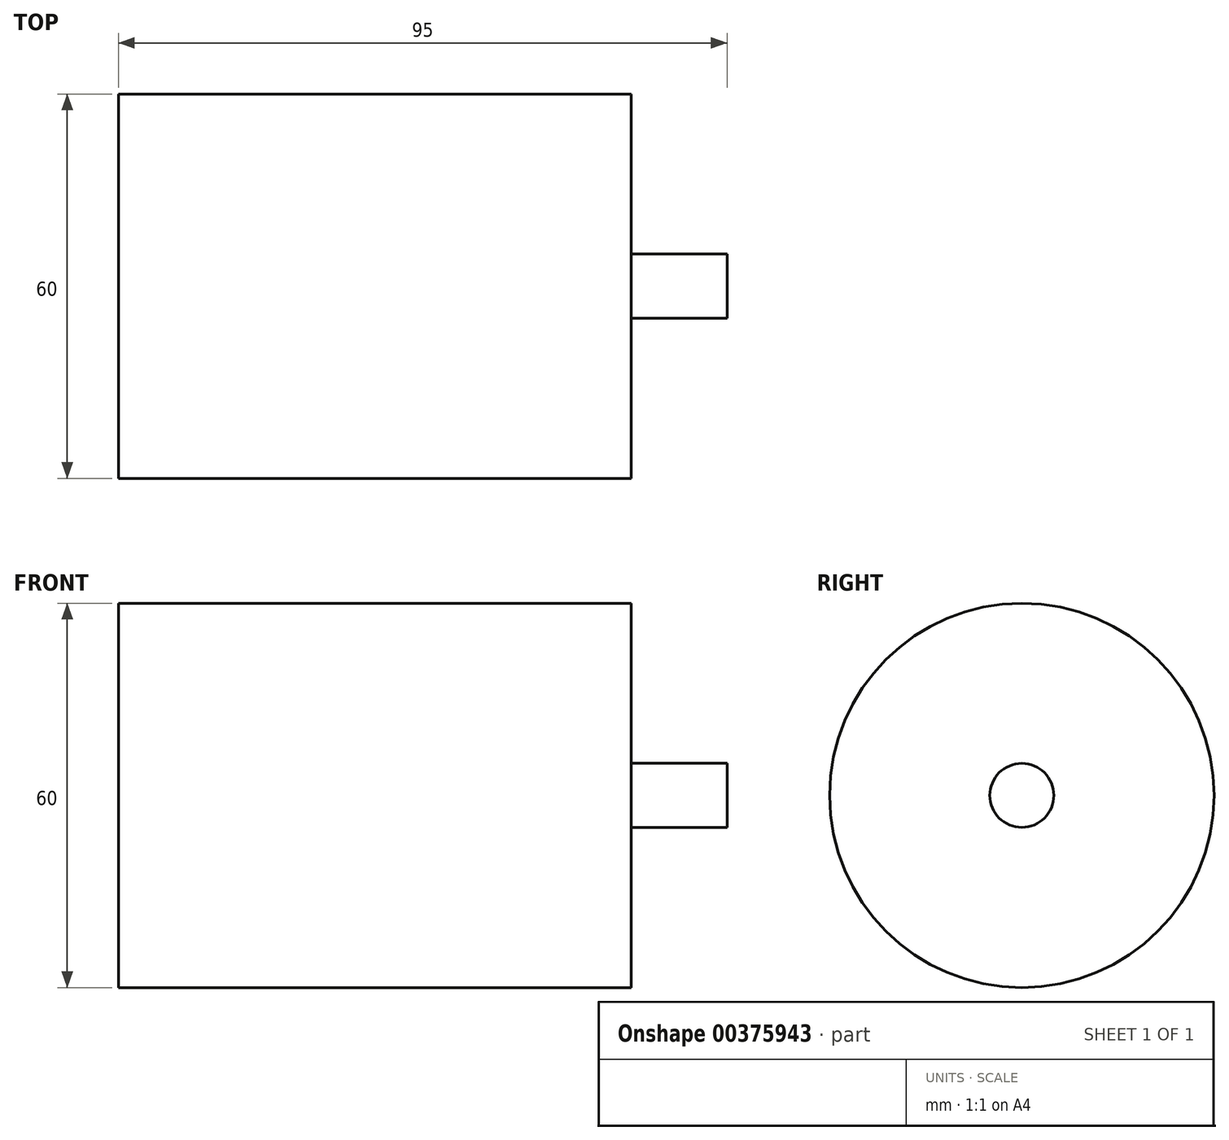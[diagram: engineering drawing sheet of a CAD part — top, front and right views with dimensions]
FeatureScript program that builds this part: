
annotation { "Feature Type Name" : "Feature", "Feature Type Description" : "" }
export const myFeature = defineFeature(function(context is Context, id is Id, definition is map)
    precondition{}
    {
        {
            var Q0;
            Q0=qCreatedBy(makeId("Front.planeOp"),FACE);
            var sketch = newSketch(context, id + "F0", { "sketchPlane" : qUnion([Q0])});
            skLineSegment(sketch, "E0", {"start": v(-119.51, 0) * mm, "end": v(134.65, 0) * mm, "construction": true});
            skLineSegment(sketch, "E1", {"start": v(0, 0) * mm, "end": v(0, 30) * mm});
            skLineSegment(sketch, "E2", {"start": v(0, 30) * mm, "end": v(80, 30) * mm});
            skLineSegment(sketch, "E3", {"start": v(80, 30) * mm, "end": v(80, 5) * mm});
            skLineSegment(sketch, "E4", {"start": v(80, 5) * mm, "end": v(95, 5) * mm});
            skLineSegment(sketch, "E5", {"start": v(95, 5) * mm, "end": v(95, 0) * mm});
            skLineSegment(sketch, "E6", {"start": v(0, 0) * mm, "end": v(95, 0) * mm});
            skSolve(sketch);
        }
        {
            var Q0;
            Q0=qSketchRegion(id+"F0",true);
            var Q1;
            Q1=sQuery(id+"F0.wireOp",EDGE,"E0");
            revolve(context, id + "F1", {"entities" : qUnion([Q0]), "axis" : qUnion([Q1]), "revolveType" : RevolveType.FULL});
        }
    });
